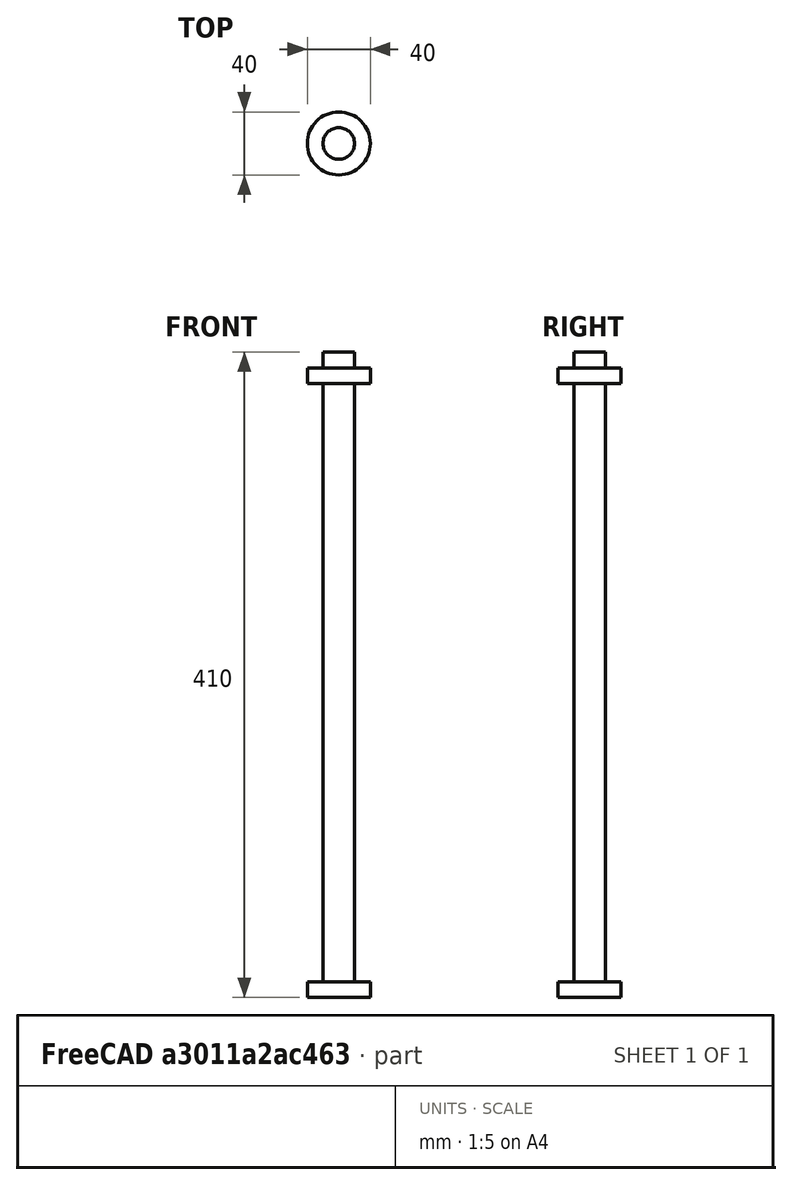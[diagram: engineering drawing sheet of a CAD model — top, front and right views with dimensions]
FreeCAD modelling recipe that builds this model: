
FCSTD DOCUMENT  (FreeCAD 0.20R29410 (Git))
Label: lk3
License: All rights reserved
LicenseURL: http://en.wikipedia.org/wiki/All_rights_reserved
objects: Sketcher::SketchObject×1, PartDesign::Revolution×1, PartDesign::Body×1, Mesh::Feature×1
note: 4 computed .brp shape members not serialized (recipe doc carries the construction recipe); baked Part::Feature solids carry a one-line shape summary decoded from their .brp

FEATURE [Sketcher::SketchObject] Sketch
  FullyConstrained = true
  MapMode = 5
  Placement = pos=(0,0,0) rot=(1,0,0;1.5708rad)
  Support = -> [XZ_Plane]
  sketch-geometry (10):
    g0: LineSegment StartX=10 StartY=-380 StartZ=0 EndX=10 EndY=0 EndZ=0
    g1: LineSegment StartX=10 StartY=0 StartZ=0 EndX=20 EndY=0 EndZ=0
    g2: LineSegment StartX=20 StartY=0 StartZ=0 EndX=20 EndY=10 EndZ=0
    g3: LineSegment StartX=20 StartY=10 StartZ=0 EndX=10 EndY=10 EndZ=0
    g4: LineSegment StartX=10 StartY=10 StartZ=0 EndX=10 EndY=20 EndZ=0
    g5: LineSegment StartX=10 StartY=20 StartZ=0 EndX=0 EndY=20 EndZ=0
    g6: LineSegment StartX=0 StartY=-390 StartZ=0 EndX=0 EndY=20 EndZ=0
    g7: LineSegment StartX=0 StartY=-390 StartZ=0 EndX=20 EndY=-390 EndZ=0
    g8: LineSegment StartX=20 StartY=-390 StartZ=0 EndX=20 EndY=-380 EndZ=0
    g9: LineSegment StartX=20 StartY=-380 StartZ=0 EndX=10 EndY=-380 EndZ=0
  constraints (29):
    c: PointOnObject(g6,g-2)
    c: Vertical(g0)
    c: Coincident(g1,g0)
    c: Coincident(g2,g1)
    c: Vertical(g2)
    c: Coincident(g3,g2)
    c: Horizontal(g3)
    c: Coincident(g4,g3)
    c: Vertical(g4)
    c: PointOnObject(g5,g-2)
    c: Horizontal(g5)
    c: Vertical(g3,g0)
    c: DistanceY(g2,g2) = 10
    c: DistanceX(g1,g1) = 10
    c: DistanceY(g6,g5) = 410
    c: Coincident(g6,g5)
    c: Tangent(g1,g-1)
    c: DistanceY(g4,g4) = 10
    c: Coincident(g4,g5)
    c: Coincident(g7,g6)
    c: Horizontal(g7)
    c: Coincident(g8,g7)
    c: Vertical(g8)
    c: Coincident(g9,g8)
    c: Horizontal(g9)
    c: Coincident(g9,g0)
    c: DistanceX(g6,g0) = 10
    c: Equal(g8,g2)
    c: Equal(g1,g9)
FEATURE [PartDesign::Revolution] Revolution
  Angle = 360
  Axis = (0,-2e-16,1)
  Base = (0,0,0)
  Placement = pos=(0,0,0) rot=(1,0,0;1.5708rad)
  Profile = -> Sketch
  ReferenceAxis = -> Sketch [V_Axis]
  Reversed = true
FEATURE [PartDesign::Body] Body
  Group = -> [Sketch,Revolution]
  Origin = -> Origin
  Tip = -> Revolution
FEATURE [Mesh::Feature] Mesh  label="Body (Meshed)"
